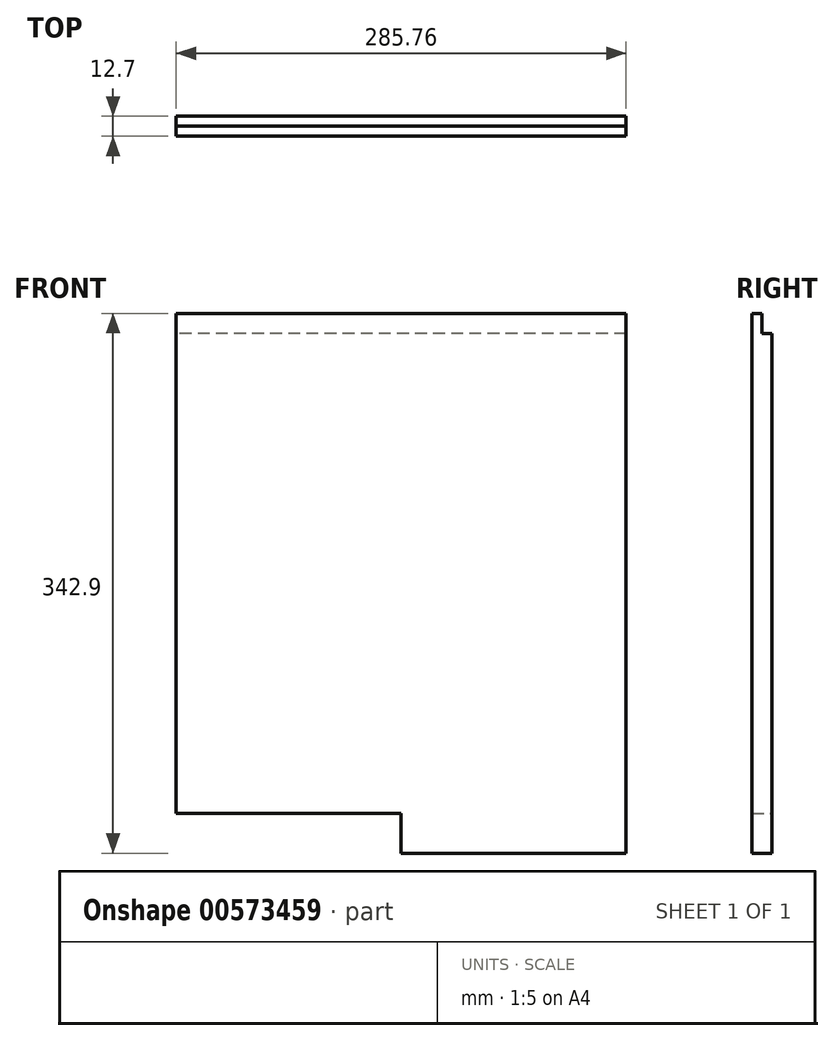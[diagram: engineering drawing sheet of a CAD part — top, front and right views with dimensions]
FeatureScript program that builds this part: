
annotation { "Feature Type Name" : "Feature", "Feature Type Description" : "" }
export const myFeature = defineFeature(function(context is Context, id is Id, definition is map)
    precondition{}
    {
        {
            var Q0;
            Q0=qCreatedBy(makeId("Front.planeOp"),FACE);
            var sketch = newSketch(context, id + "F0", { "sketchPlane" : qUnion([Q0])});
            skLineSegment(sketch, "E0.bottom", {"start": v(142.87, 171.45) * mm, "end": v(-142.88, 171.45) * mm});
            skLineSegment(sketch, "E0.top", {"start": v(142.88, -171.45) * mm, "end": v(-142.87, -171.45) * mm});
            skLineSegment(sketch, "E0.left", {"start": v(142.87, 171.45) * mm, "end": v(142.88, -171.45) * mm});
            skLineSegment(sketch, "E0.right", {"start": v(-142.88, 171.45) * mm, "end": v(-142.87, -171.45) * mm});
            skPoint(sketch, "E0.middle", {"position": v(0, 0) * mm});
            skSolve(sketch);
        }
        {
            var Q0;
            Q0=makeQuery(id+"F0.imprint","IMPRINT",FACE,{"disambiguationData":[TD([[makeQuery(id+"F0.imprint","IMPRINT",EDGE,{"derivedFrom":sQuery(id+"F0.wireOp",EDGE,"E0.bottom")}),1.0]])]});
            extrude(context, id + "F1", {"entities" : qUnion([Q0]), "depth" : 12.7 * mm, "offsetDistance" : 25.4 * mm});
        }
        {
            var Q0;
            Q0=makeQuery(id+"F1.opExtrude","SWEPT_FACE",FACE,{"disambiguationData":[OSD([sQuery(id+"F0.wireOp",EDGE,"E0.top")])]});
            var sketch = newSketch(context, id + "F2", { "sketchPlane" : qUnion([Q0])});
            skLineSegment(sketch, "E1.bottom", {"start": v(-142.87, 0) * mm, "end": v(0, 0) * mm});
            skLineSegment(sketch, "E1.top", {"start": v(-142.87, 12.7) * mm, "end": v(0, 12.7) * mm});
            skLineSegment(sketch, "E1.left", {"start": v(-142.87, 0) * mm, "end": v(-142.87, 12.7) * mm});
            skLineSegment(sketch, "E1.right", {"start": v(0, 0) * mm, "end": v(0, 12.7) * mm});
            skSolve(sketch);
        }
        {
            var Q0;
            Q0=makeQuery(id+"F2.imprint","IMPRINT",FACE,{"disambiguationData":[TD([[makeQuery(id+"F2.imprint","IMPRINT",EDGE,{"derivedFrom":sQuery(id+"F2.wireOp",EDGE,"E1.bottom")}),-1.0]])]});
            extrude(context, id + "F3", {"entities" : qUnion([Q0]), "operationType" : NewBodyOperationType.REMOVE, "oppositeDirection" : true, "depth" : 25.4 * mm, "offsetDistance" : 25.4 * mm});
        }
        {
            var Q0;
            Q0=makeQuery(id+"F1.opExtrude","SWEPT_FACE",FACE,{"disambiguationData":[OSD([sQuery(id+"F0.wireOp",EDGE,"E0.bottom")])]});
            var sketch = newSketch(context, id + "F4", { "sketchPlane" : qUnion([Q0])});
            skLineSegment(sketch, "E2.bottom", {"start": v(-142.88, 0) * mm, "end": v(142.87, 0) * mm});
            skLineSegment(sketch, "E2.top", {"start": v(-142.88, -6.35) * mm, "end": v(142.87, -6.35) * mm});
            skLineSegment(sketch, "E2.left", {"start": v(-142.88, 0) * mm, "end": v(-142.88, -6.35) * mm});
            skLineSegment(sketch, "E2.right", {"start": v(142.87, 0) * mm, "end": v(142.87, -6.35) * mm});
            skSolve(sketch);
        }
        {
            var Q0;
            Q0=makeQuery(id+"F4.imprint","IMPRINT",FACE,{"disambiguationData":[TD([[makeQuery(id+"F4.imprint","IMPRINT",EDGE,{"derivedFrom":sQuery(id+"F4.wireOp",EDGE,"E2.bottom")}),1.0]])]});
            extrude(context, id + "F5", {"entities" : qUnion([Q0]), "operationType" : NewBodyOperationType.REMOVE, "oppositeDirection" : true, "depth" : 12.7 * mm, "offsetDistance" : 25.4 * mm});
        }
    });
